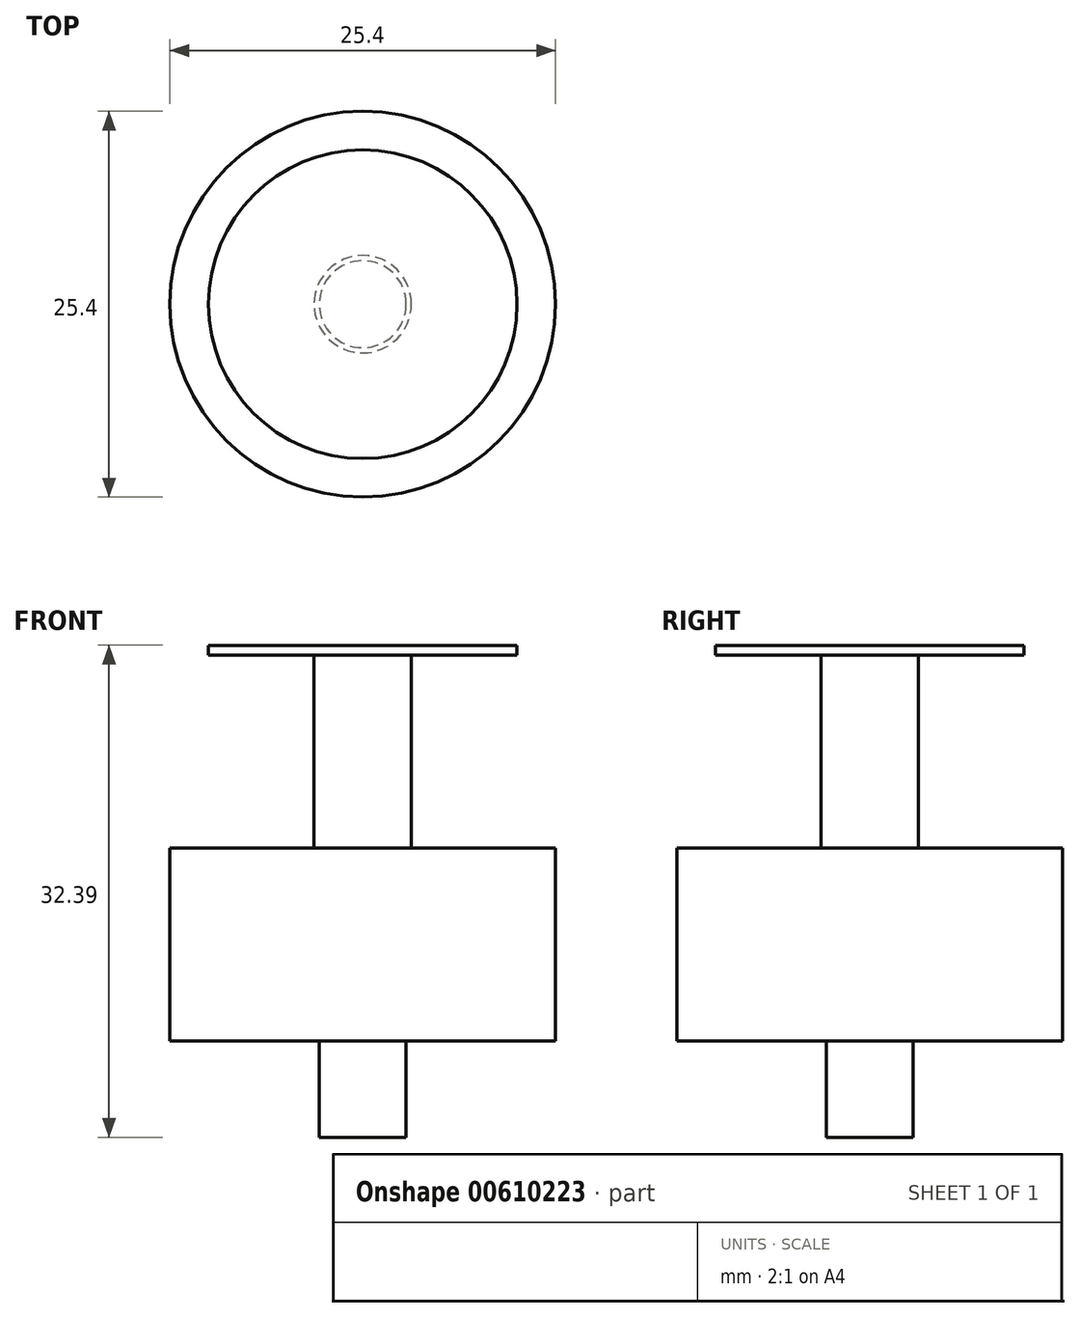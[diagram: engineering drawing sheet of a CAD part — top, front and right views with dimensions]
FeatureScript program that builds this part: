
annotation { "Feature Type Name" : "Feature", "Feature Type Description" : "" }
export const myFeature = defineFeature(function(context is Context, id is Id, definition is map)
    precondition{}
    {
        {
            var Q0;
            Q0=qCreatedBy(makeId("Top.planeOp"),FACE);
            var sketch = newSketch(context, id + "F0", { "sketchPlane" : qUnion([Q0])});
            skCircle(sketch, "E0", {"center": v(0, 0) * mm, "radius": 12.7 * mm});
            skSolve(sketch);
        }
        {
            var Q0;
            Q0=makeQuery(id+"F0.imprint","IMPRINT",FACE,{"disambiguationData":[TD([[makeQuery(id+"F0.imprint","IMPRINT",EDGE,{"derivedFrom":sQuery(id+"F0.wireOp",EDGE,"E0")}),1.0]])]});
            extrude(context, id + "F1", {"entities" : qUnion([Q0]), "depth" : 12.7 * mm, "offsetDistance" : 25.4 * mm});
        }
        {
            var Q0;
            Q0=makeQuery(id+"F1.opExtrude","CAP_FACE",FACE,{"disambiguationData":[OSD([sQuery(id+"F0.wireOp",EDGE,"E0")])],"isStart":false});
            var sketch = newSketch(context, id + "F2", { "sketchPlane" : qUnion([Q0])});
            skCircle(sketch, "E1", {"center": v(0, 0) * mm, "radius": 3.2 * mm});
            skSolve(sketch);
        }
        {
            var Q0;
            Q0=makeQuery(id+"F2.imprint","IMPRINT",FACE,{"disambiguationData":[TD([[makeQuery(id+"F2.imprint","IMPRINT",EDGE,{"derivedFrom":sQuery(id+"F2.wireOp",EDGE,"E1")}),1.0]])]});
            extrude(context, id + "F3", {"entities" : qUnion([Q0]), "operationType" : NewBodyOperationType.ADD, "depth" : 12.7 * mm, "offsetDistance" : 25.4 * mm});
        }
        {
            var Q0;
            Q0=makeQuery(id+"F3.opExtrude","CAP_FACE",FACE,{"disambiguationData":[OSD([sQuery(id+"F2.wireOp",EDGE,"E1")])],"isStart":false});
            var sketch = newSketch(context, id + "F4", { "sketchPlane" : qUnion([Q0])});
            skCircle(sketch, "E2", {"center": v(0, 0) * mm, "radius": 10.16 * mm});
            skSolve(sketch);
        }
        {
            var Q0;
            Q0 = qSketchRegion(id + "F4", true);
            extrude(context, id + "F5", {"entities" : qUnion([Q0]), "operationType" : NewBodyOperationType.ADD, "depth" : 0.64 * mm, "offsetDistance" : 25.4 * mm});
        }
        {
            var Q0;
            Q0=makeQuery(id+"F1.opExtrude","CAP_FACE",FACE,{"disambiguationData":[OSD([sQuery(id+"F0.wireOp",EDGE,"E0")])],"isStart":true});
            var sketch = newSketch(context, id + "F6", { "sketchPlane" : qUnion([Q0])});
            skCircle(sketch, "E3", {"center": v(0, 0) * mm, "radius": 2.86 * mm});
            skSolve(sketch);
        }
        {
            var Q0;
            Q0=makeQuery(id+"F6.imprint","IMPRINT",FACE,{"disambiguationData":[TD([[makeQuery(id+"F6.imprint","IMPRINT",EDGE,{"derivedFrom":sQuery(id+"F6.wireOp",EDGE,"E3")}),1.0]])]});
            extrude(context, id + "F7", {"entities" : qUnion([Q0]), "operationType" : NewBodyOperationType.ADD, "depth" : 6.35 * mm, "offsetDistance" : 25.4 * mm});
        }
    });
